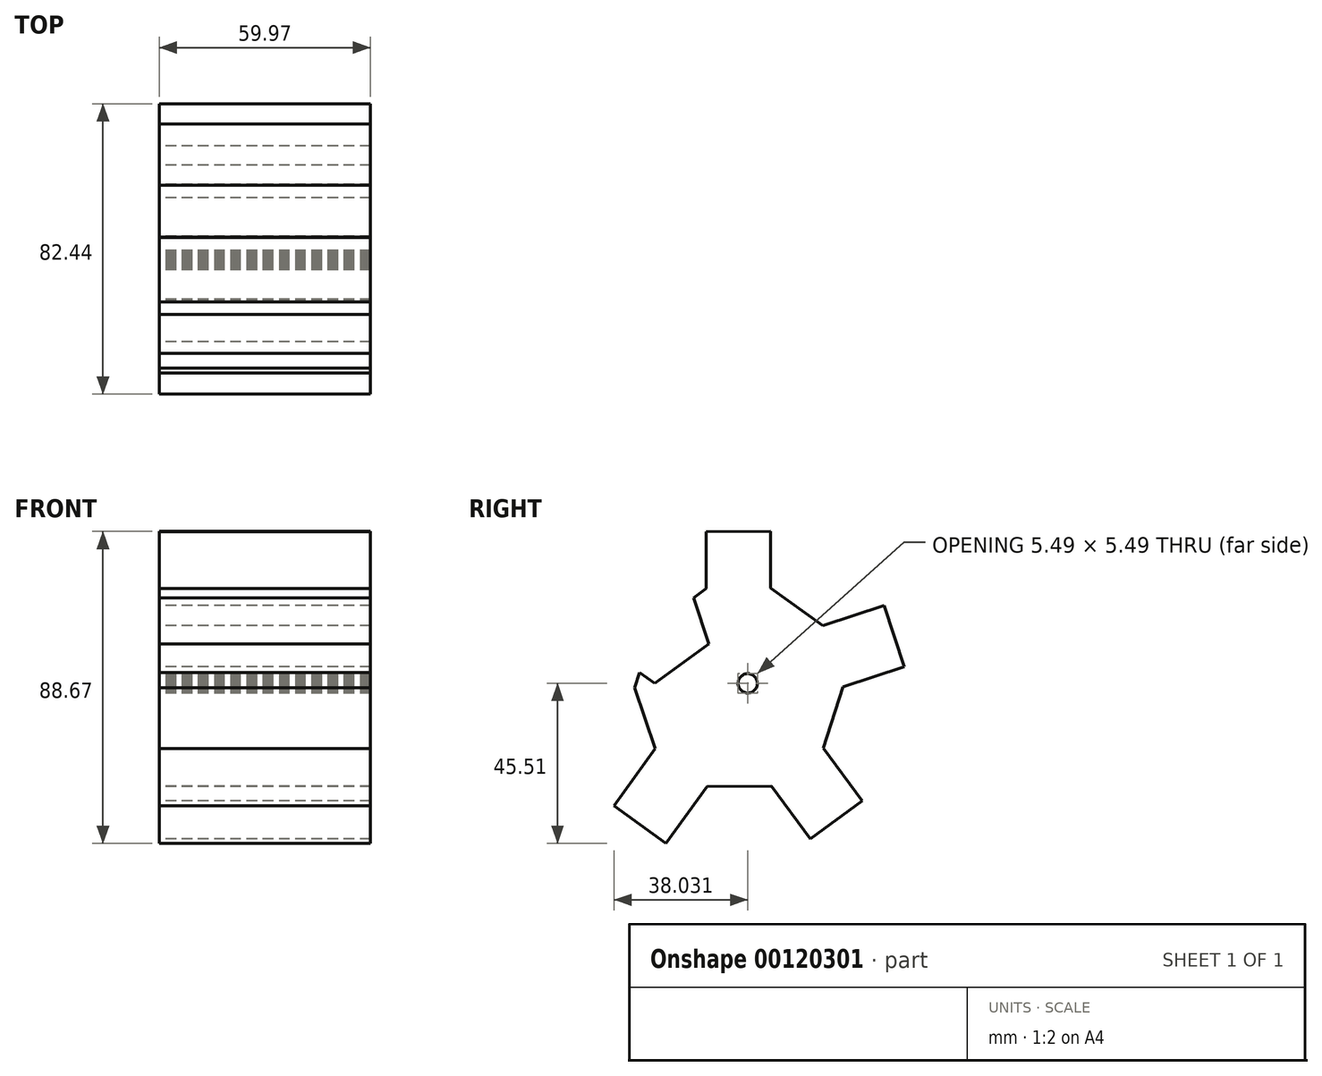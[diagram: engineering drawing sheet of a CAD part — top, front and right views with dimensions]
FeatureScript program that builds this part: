
annotation { "Feature Type Name" : "Feature", "Feature Type Description" : "" }
export const myFeature = defineFeature(function(context is Context, id is Id, definition is map)
    precondition{}
    {
        {
            var Q0;
            Q0=qCreatedBy(makeId("Right.planeOp"),FACE);
            var sketch = newSketch(context, id + "F0", { "sketchPlane" : qUnion([Q0])});
            skCircle(sketch, "E0.cCircle", {"center": v(43.14, 43) * mm, "radius": 28.11 * mm, "construction": true});
            skLineSegment(sketch, "E0.0", {"start": v(34.13, 14.84) * mm, "end": v(19.3, 25.51) * mm});
            skLineSegment(sketch, "E0.1", {"start": v(19.3, 25.51) * mm, "end": v(13.58, 42.86) * mm});
            skLineSegment(sketch, "E0.2", {"start": v(13.58, 42.86) * mm, "end": v(19.14, 60.26) * mm});
            skLineSegment(sketch, "E0.3", {"start": v(19.14, 60.26) * mm, "end": v(33.87, 71.07) * mm});
            skLineSegment(sketch, "E0.4", {"start": v(33.87, 71.07) * mm, "end": v(52.14, 71.15) * mm});
            skLineSegment(sketch, "E0.5", {"start": v(52.14, 71.15) * mm, "end": v(66.97, 60.48) * mm});
            skLineSegment(sketch, "E0.6", {"start": v(66.97, 60.48) * mm, "end": v(72.7, 43.13) * mm});
            skLineSegment(sketch, "E0.7", {"start": v(72.7, 43.13) * mm, "end": v(67.13, 25.73) * mm});
            skLineSegment(sketch, "E0.8", {"start": v(67.13, 25.73) * mm, "end": v(52.4, 14.93) * mm});
            skLineSegment(sketch, "E0.9", {"start": v(52.4, 14.93) * mm, "end": v(34.13, 14.84) * mm});
            skPoint(sketch, "E0.0.midPoint", {"position": v(26.72, 20.18) * mm});
            skCircle(sketch, "E1.cCircle", {"center": v(45.64, 44.1) * mm, "radius": 2.74 * mm, "construction": true});
            skLineSegment(sketch, "E1.0", {"start": v(43.2, 42.84) * mm, "end": v(43.07, 43.15) * mm});
            skLineSegment(sketch, "E1.1", {"start": v(43.07, 43.15) * mm, "end": v(42.97, 43.48) * mm});
            skLineSegment(sketch, "E1.2", {"start": v(42.97, 43.48) * mm, "end": v(42.9, 43.82) * mm});
            skLineSegment(sketch, "E1.3", {"start": v(42.9, 43.82) * mm, "end": v(42.9, 44.17) * mm});
            skLineSegment(sketch, "E1.4", {"start": v(42.9, 44.17) * mm, "end": v(42.92, 44.51) * mm});
            skLineSegment(sketch, "E1.5", {"start": v(42.92, 44.51) * mm, "end": v(43, 44.85) * mm});
            skLineSegment(sketch, "E1.6", {"start": v(43, 44.85) * mm, "end": v(43.1, 45.18) * mm});
            skLineSegment(sketch, "E1.7", {"start": v(43.1, 45.18) * mm, "end": v(43.26, 45.48) * mm});
            skLineSegment(sketch, "E1.8", {"start": v(43.26, 45.48) * mm, "end": v(43.45, 45.77) * mm});
            skLineSegment(sketch, "E1.9", {"start": v(43.45, 45.77) * mm, "end": v(43.68, 46.03) * mm});
            skLineSegment(sketch, "E1.10", {"start": v(43.68, 46.03) * mm, "end": v(43.94, 46.26) * mm});
            skLineSegment(sketch, "E1.11", {"start": v(43.94, 46.26) * mm, "end": v(44.22, 46.46) * mm});
            skLineSegment(sketch, "E1.12", {"start": v(44.22, 46.46) * mm, "end": v(44.53, 46.62) * mm});
            skLineSegment(sketch, "E1.13", {"start": v(44.53, 46.62) * mm, "end": v(44.85, 46.74) * mm});
            skLineSegment(sketch, "E1.14", {"start": v(44.85, 46.74) * mm, "end": v(45.18, 46.82) * mm});
            skLineSegment(sketch, "E1.15", {"start": v(45.18, 46.82) * mm, "end": v(45.53, 46.85) * mm});
            skLineSegment(sketch, "E1.16", {"start": v(45.53, 46.85) * mm, "end": v(45.87, 46.85) * mm});
            skLineSegment(sketch, "E1.17", {"start": v(45.87, 46.85) * mm, "end": v(46.21, 46.8) * mm});
            skLineSegment(sketch, "E1.18", {"start": v(46.21, 46.8) * mm, "end": v(46.55, 46.7) * mm});
            skLineSegment(sketch, "E1.19", {"start": v(46.55, 46.7) * mm, "end": v(46.86, 46.57) * mm});
            skLineSegment(sketch, "E1.20", {"start": v(46.86, 46.57) * mm, "end": v(47.16, 46.4) * mm});
            skLineSegment(sketch, "E1.21", {"start": v(47.16, 46.4) * mm, "end": v(47.44, 46.19) * mm});
            skLineSegment(sketch, "E1.22", {"start": v(47.44, 46.19) * mm, "end": v(47.68, 45.95) * mm});
            skLineSegment(sketch, "E1.23", {"start": v(47.68, 45.95) * mm, "end": v(47.9, 45.68) * mm});
            skLineSegment(sketch, "E1.24", {"start": v(47.9, 45.68) * mm, "end": v(48.08, 45.38) * mm});
            skLineSegment(sketch, "E1.25", {"start": v(48.08, 45.38) * mm, "end": v(48.22, 45.07) * mm});
            skLineSegment(sketch, "E1.26", {"start": v(48.22, 45.07) * mm, "end": v(48.31, 44.74) * mm});
            skLineSegment(sketch, "E1.27", {"start": v(48.31, 44.74) * mm, "end": v(48.37, 44.4) * mm});
            skLineSegment(sketch, "E1.28", {"start": v(48.37, 44.4) * mm, "end": v(48.39, 44.05) * mm});
            skLineSegment(sketch, "E1.29", {"start": v(48.39, 44.05) * mm, "end": v(48.36, 43.7) * mm});
            skLineSegment(sketch, "E1.30", {"start": v(48.36, 43.7) * mm, "end": v(48.29, 43.37) * mm});
            skLineSegment(sketch, "E1.31", {"start": v(48.29, 43.37) * mm, "end": v(48.17, 43.04) * mm});
            skLineSegment(sketch, "E1.32", {"start": v(48.17, 43.04) * mm, "end": v(48.02, 42.74) * mm});
            skLineSegment(sketch, "E1.33", {"start": v(48.02, 42.74) * mm, "end": v(47.83, 42.45) * mm});
            skLineSegment(sketch, "E1.34", {"start": v(47.83, 42.45) * mm, "end": v(47.6, 42.19) * mm});
            skLineSegment(sketch, "E1.35", {"start": v(47.6, 42.19) * mm, "end": v(47.34, 41.96) * mm});
            skLineSegment(sketch, "E1.36", {"start": v(47.34, 41.96) * mm, "end": v(47.06, 41.76) * mm});
            skLineSegment(sketch, "E1.37", {"start": v(47.06, 41.76) * mm, "end": v(46.76, 41.6) * mm});
            skLineSegment(sketch, "E1.38", {"start": v(46.76, 41.6) * mm, "end": v(46.43, 41.48) * mm});
            skLineSegment(sketch, "E1.39", {"start": v(46.43, 41.48) * mm, "end": v(46.1, 41.4) * mm});
            skLineSegment(sketch, "E1.40", {"start": v(46.1, 41.4) * mm, "end": v(45.75, 41.37) * mm});
            skLineSegment(sketch, "E1.41", {"start": v(45.75, 41.37) * mm, "end": v(45.4, 41.37) * mm});
            skLineSegment(sketch, "E1.42", {"start": v(45.4, 41.37) * mm, "end": v(45.07, 41.42) * mm});
            skLineSegment(sketch, "E1.43", {"start": v(45.07, 41.42) * mm, "end": v(44.74, 41.52) * mm});
            skLineSegment(sketch, "E1.44", {"start": v(44.74, 41.52) * mm, "end": v(44.42, 41.65) * mm});
            skLineSegment(sketch, "E1.45", {"start": v(44.42, 41.65) * mm, "end": v(44.12, 41.82) * mm});
            skLineSegment(sketch, "E1.46", {"start": v(44.12, 41.82) * mm, "end": v(43.84, 42.03) * mm});
            skLineSegment(sketch, "E1.47", {"start": v(43.84, 42.03) * mm, "end": v(43.6, 42.27) * mm});
            skLineSegment(sketch, "E1.48", {"start": v(43.6, 42.27) * mm, "end": v(43.38, 42.54) * mm});
            skLineSegment(sketch, "E1.49", {"start": v(43.38, 42.54) * mm, "end": v(43.2, 42.84) * mm});
            skCircle(sketch, "E2.cCircle", {"center": v(19.14, 60.26) * mm, "radius": 13.1 * mm, "construction": true});
            skLineSegment(sketch, "E2.0", {"start": v(3.76, 55.19) * mm, "end": v(9.56, 73.32) * mm});
            skLineSegment(sketch, "E2.1", {"start": v(9.56, 73.32) * mm, "end": v(28.6, 73.4) * mm});
            skLineSegment(sketch, "E2.2", {"start": v(28.6, 73.4) * mm, "end": v(34.57, 55.33) * mm});
            skLineSegment(sketch, "E2.3", {"start": v(34.57, 55.33) * mm, "end": v(19.22, 44.07) * mm});
            skLineSegment(sketch, "E2.4", {"start": v(19.22, 44.07) * mm, "end": v(3.76, 55.19) * mm});
            skPoint(sketch, "E2.0.midPoint", {"position": v(6.66, 64.25) * mm});
            skSolve(sketch);
        }
        {
            var Q0;
            Q0=makeQuery(id+"F0.imprint","IMPRINT",FACE,{"disambiguationData":[TD([[makeQuery(id+"F0.imprint","IMPRINT",EDGE,{"derivedFrom":sQuery(id+"F0.wireOp",EDGE,"E0.0")}),-1.0]])]});
            extrude(context, id + "F1", {"entities" : qUnion([Q0]), "depth" : 59.97 * mm});
        }
        {
            var Q0;
            Q0=makeQuery(id+"F1.opExtrude","SWEPT_FACE",FACE,{"disambiguationData":[OSD([sQuery(id+"F0.wireOp",EDGE,"E0.4")])]});
            extrude(context, id + "F2", {"entities" : qUnion([Q0]), "operationType" : NewBodyOperationType.ADD, "depth" : 16.12 * mm});
        }
        {
            var Q0;
            Q0=makeQuery(id+"F1.opExtrude","SWEPT_FACE",FACE,{"disambiguationData":[OSD([sQuery(id+"F0.wireOp",EDGE,"E0.6")])]});
            extrude(context, id + "F3", {"entities" : qUnion([Q0]), "operationType" : NewBodyOperationType.ADD, "depth" : 18.28 * mm});
        }
        {
            var Q0;
            Q0=makeQuery(id+"F1.opExtrude","SWEPT_FACE",FACE,{"disambiguationData":[OSD([sQuery(id+"F0.wireOp",EDGE,"E0.8")])]});
            extrude(context, id + "F4", {"entities" : qUnion([Q0]), "operationType" : NewBodyOperationType.ADD, "depth" : 18.66 * mm});
        }
        {
            var Q0;
            Q0=makeQuery(id+"F1.opExtrude","SWEPT_FACE",FACE,{"disambiguationData":[OSD([sQuery(id+"F0.wireOp",EDGE,"E0.0")])]});
            extrude(context, id + "F5", {"entities" : qUnion([Q0]), "operationType" : NewBodyOperationType.ADD, "depth" : 20.01 * mm});
        }
    });
